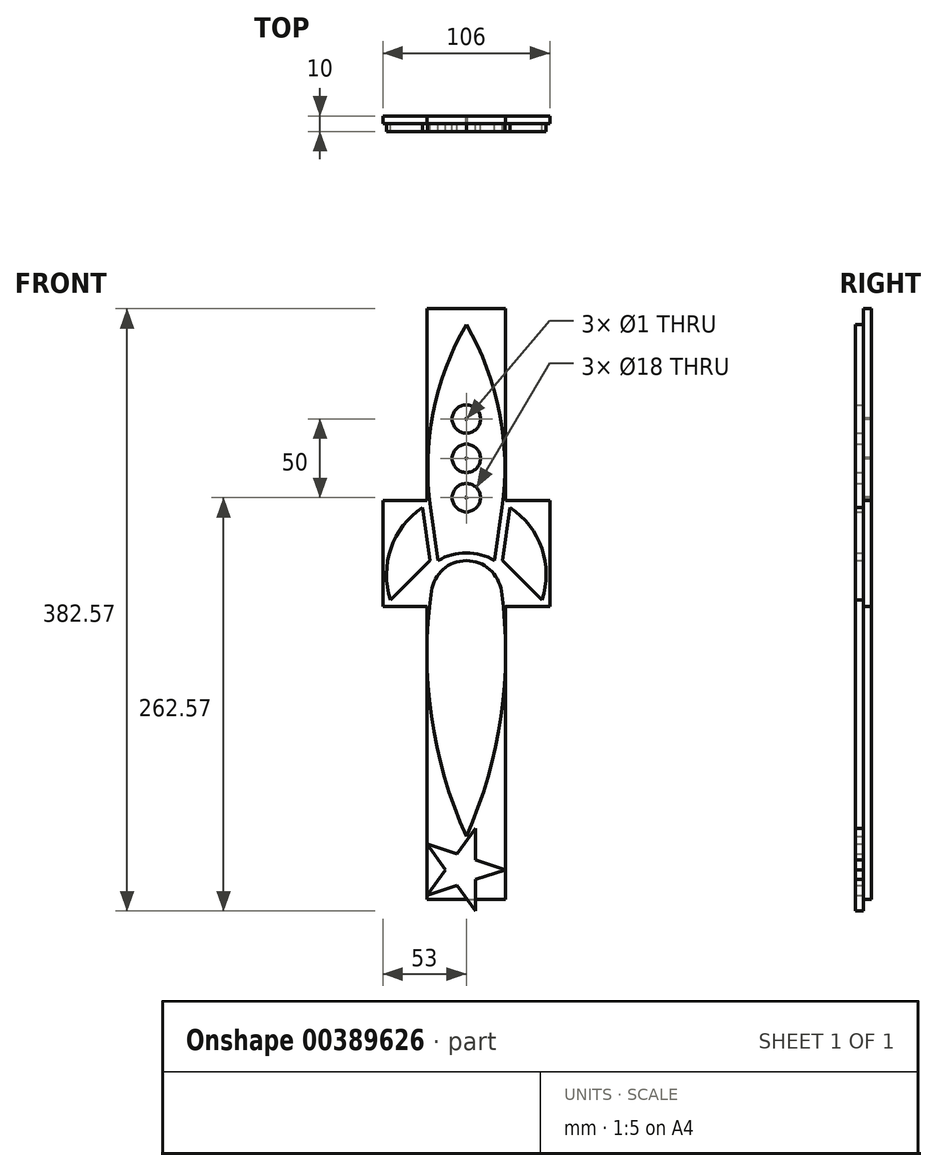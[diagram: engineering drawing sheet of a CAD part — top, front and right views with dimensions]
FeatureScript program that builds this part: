
annotation { "Feature Type Name" : "Feature", "Feature Type Description" : "" }
export const myFeature = defineFeature(function(context is Context, id is Id, definition is map)
    precondition{}
    {
        {
            var Q0;
            Q0=qCreatedBy(makeId("Front.planeOp"),FACE);
            var sketch = newSketch(context, id + "F0", { "sketchPlane" : qUnion([Q0])});
            skLineSegment(sketch, "E0.top", {"start": v(180, 0) * mm, "end": v(229, 0) * mm, "construction": true});
            skLineSegment(sketch, "E0.left", {"start": v(180, 117.37) * mm, "end": v(180, 0) * mm, "construction": true});
            skLineSegment(sketch, "E0.right", {"start": v(229, 157) * mm, "end": v(229, 0) * mm, "construction": true});
            skPoint(sketch, "E1", {"position": v(204.5, 0) * mm});
            skLineSegment(sketch, "E2", {"start": v(204.5, 0) * mm, "end": v(204.5, 155.05) * mm, "construction": true});
            skCircle(sketch, "E3", {"center": v(204.5, 115) * mm, "radius": 9 * mm});
            skCircle(sketch, "E4", {"center": v(204.5, 90) * mm, "radius": 9 * mm});
            skCircle(sketch, "E5", {"center": v(204.5, 65) * mm, "radius": 9 * mm});
            skArc(sketch, "E6", {"start": v(222.5, 25) * mm, "mid": v(204.5, 29.98) * mm, "end": v(186.5, 25) * mm});
            skLineSegment(sketch, "E7", {"start": v(186.5, 25) * mm, "end": v(181.77, 58.68) * mm});
            skArc(sketch, "E8", {"start": v(204.5, 175) * mm, "mid": v(183.37, 118.75) * mm, "end": v(181.77, 58.68) * mm});
            skPoint(sketch, "E9", {"position": v(180, 58.68) * mm});
            skArc(sketch, "E10.MirrorCS", {"start": v(204.5, 175) * mm, "mid": v(225.63, 118.75) * mm, "end": v(227.23, 58.68) * mm});
            skLineSegment(sketch, "E11.MirrorCS", {"start": v(222.5, 25) * mm, "end": v(227.23, 58.68) * mm});
            skLineSegment(sketch, "E12.0", {"start": v(227.55, 25) * mm, "end": v(232.28, 58.68) * mm});
            skLineSegment(sketch, "E13", {"start": v(227.55, 25) * mm, "end": v(252.55, 0) * mm});
            skArc(sketch, "E14", {"start": v(252.55, 0) * mm, "mid": v(252.44, 32.8) * mm, "end": v(232.28, 58.68) * mm});
            skArc(sketch, "E15", {"start": v(226.75, 5.66) * mm, "mid": v(219.24, 19.49) * mm, "end": v(204.5, 25) * mm});
            skArc(sketch, "E16", {"start": v(204.5, -150) * mm, "mid": v(226.65, -73.75) * mm, "end": v(226.75, 5.66) * mm});
            skLineSegment(sketch, "E17", {"start": v(204.5, 2.53) * mm, "end": v(226.75, 5.66) * mm, "construction": true});
            skArc(sketch, "E18.MirrorCS", {"start": v(204.5, -150) * mm, "mid": v(182.35, -73.75) * mm, "end": v(182.25, 5.66) * mm});
            skArc(sketch, "E19.MirrorCS", {"start": v(182.25, 5.66) * mm, "mid": v(189.76, 19.49) * mm, "end": v(204.5, 25) * mm});
            skLineSegment(sketch, "E20.MirrorCS", {"start": v(181.45, 25) * mm, "end": v(156.45, 0) * mm});
            skLineSegment(sketch, "E21.MirrorCS", {"start": v(181.45, 25) * mm, "end": v(176.72, 58.68) * mm});
            skArc(sketch, "E22.MirrorCS", {"start": v(156.45, 0) * mm, "mid": v(156.56, 32.8) * mm, "end": v(176.72, 58.68) * mm});
            skLineSegment(sketch, "E23", {"start": v(229.5, -5.68) * mm, "end": v(229.5, -53.7) * mm, "construction": true});
            skSolve(sketch);
        }
        {
            var Q0;
            Q0 = qSketchRegion(id + "F0", true);
            extrude(context, id + "F1", {"entities" : qUnion([Q0]), "depth" : 5 * mm});
        }
        {
            var Q0;
            Q0=qCreatedBy(makeId("Front.planeOp"),FACE);
            var sketch = newSketch(context, id + "F2", { "sketchPlane" : qUnion([Q0])});
            skLineSegment(sketch, "E24.bottom", {"start": v(179.5, 185) * mm, "end": v(229.5, 185) * mm});
            skLineSegment(sketch, "E24.top", {"start": v(179.5, -190) * mm, "end": v(229.5, -190) * mm});
            skLineSegment(sketch, "E24.left", {"start": v(179.5, 185) * mm, "end": v(179.5, -190) * mm});
            skLineSegment(sketch, "E24.right", {"start": v(229.5, 185) * mm, "end": v(229.5, -190) * mm});
            skLineSegment(sketch, "E25", {"start": v(204.5, 185) * mm, "end": v(204.5, -190) * mm, "construction": true});
            skCircle(sketch, "E26", {"center": v(204.5, 115) * mm, "radius": 0.5 * mm});
            skCircle(sketch, "E27", {"center": v(204.5, 90) * mm, "radius": 0.5 * mm});
            skCircle(sketch, "E28", {"center": v(204.5, 65) * mm, "radius": 0.5 * mm});
            skLineSegment(sketch, "E29", {"start": v(229.5, 63.19) * mm, "end": v(257.5, 63.19) * mm});
            skLineSegment(sketch, "E30", {"start": v(257.5, 63.19) * mm, "end": v(257.5, -4.22) * mm});
            skLineSegment(sketch, "E31", {"start": v(257.5, -4.22) * mm, "end": v(229.5, -4.22) * mm});
            skLineSegment(sketch, "E32.MirrorCS", {"start": v(151.5, -4.22) * mm, "end": v(179.5, -4.22) * mm});
            skLineSegment(sketch, "E33.MirrorCS", {"start": v(151.5, 63.19) * mm, "end": v(151.5, -4.22) * mm});
            skLineSegment(sketch, "E34.MirrorCS", {"start": v(179.5, 63.19) * mm, "end": v(151.5, 63.19) * mm});
            skSolve(sketch);
        }
        {
            var Q0;
            Q0 = qSketchRegion(id + "F2", true);
            extrude(context, id + "F3", {"entities" : qUnion([Q0]), "oppositeDirection" : true, "depth" : 5 * mm});
        }
        {
            var Q0;
            Q0=qCreatedBy(makeId("Front.planeOp"),FACE);
            var sketch = newSketch(context, id + "F4", { "sketchPlane" : qUnion([Q0])});
            skLineSegment(sketch, "E35", {"start": v(179.5, -155.04) * mm, "end": v(198.6, -161.25) * mm});
            skLineSegment(sketch, "E36", {"start": v(229.5, -171.29) * mm, "end": v(210.4, -177.5) * mm});
            skLineSegment(sketch, "E37", {"start": v(179.5, -187.53) * mm, "end": v(191.3, -171.29) * mm});
            skLineSegment(sketch, "E38", {"start": v(210.4, -145) * mm, "end": v(210.4, -165.08) * mm});
            skLineSegment(sketch, "E39", {"start": v(210.4, -197.57) * mm, "end": v(198.6, -181.33) * mm});
            skLineSegment(sketch, "E40.trimOffspring", {"start": v(210.4, -165.08) * mm, "end": v(229.5, -171.29) * mm});
            skLineSegment(sketch, "E41.trimOffspring", {"start": v(198.6, -161.25) * mm, "end": v(210.4, -145) * mm});
            skLineSegment(sketch, "E42.trimOffspring", {"start": v(210.4, -177.5) * mm, "end": v(210.4, -197.57) * mm});
            skLineSegment(sketch, "E43.trimOffspring", {"start": v(198.6, -181.33) * mm, "end": v(179.5, -187.53) * mm});
            skLineSegment(sketch, "E44.trimOffspring", {"start": v(191.3, -171.29) * mm, "end": v(179.5, -155.04) * mm});
            skSolve(sketch);
        }
        {
            var Q0;
            Q0 = qSketchRegion(id + "F4", true);
            extrude(context, id + "F5", {"entities" : qUnion([Q0]), "operationType" : NewBodyOperationType.ADD, "depth" : 5 * mm});
        }
    });
